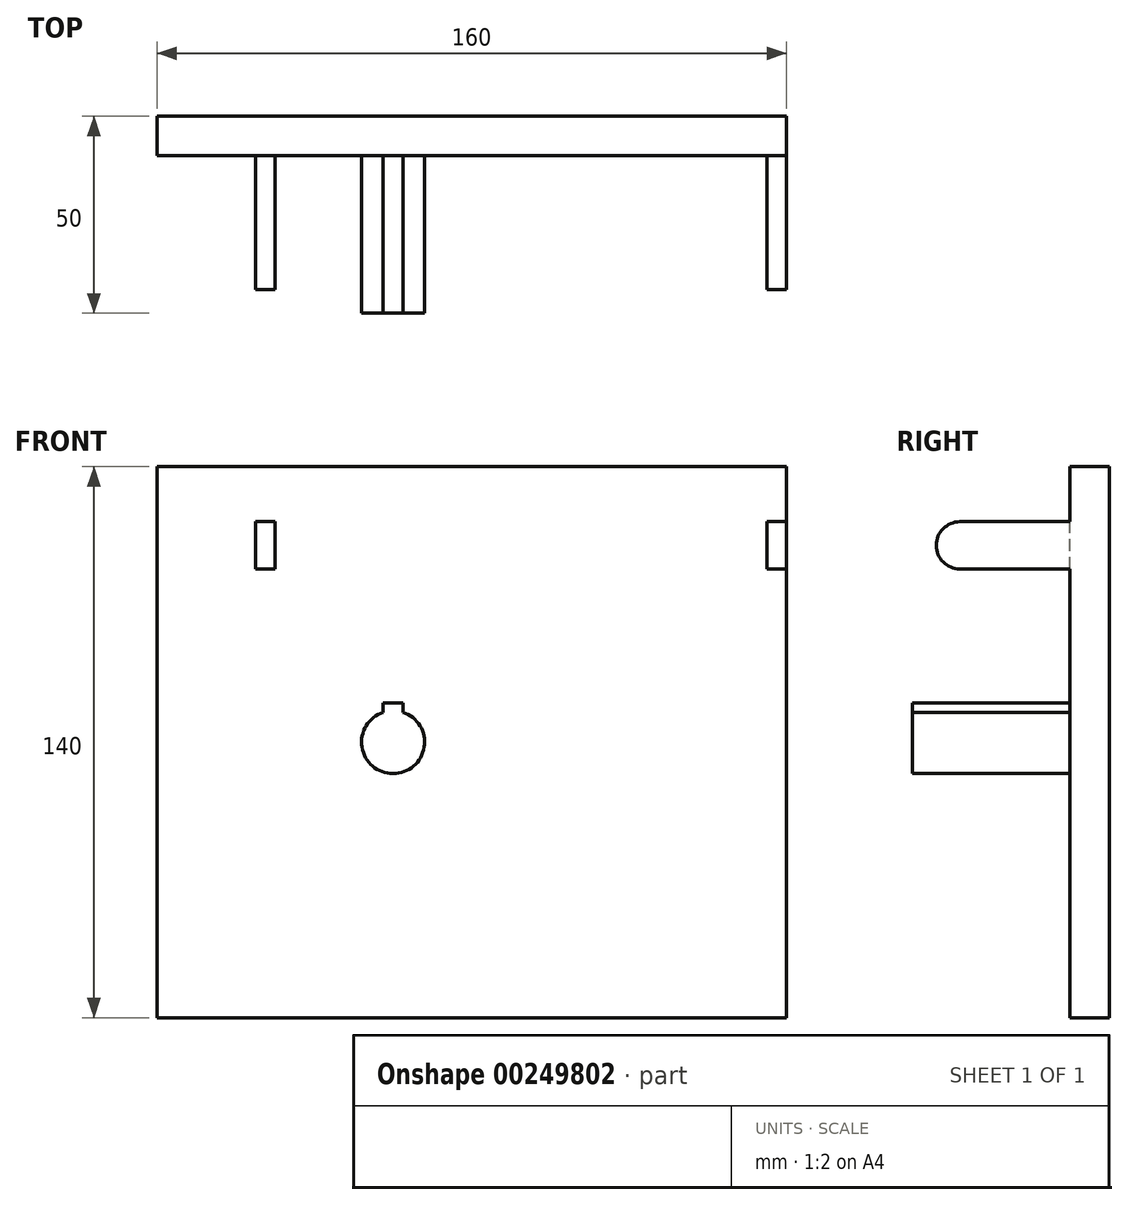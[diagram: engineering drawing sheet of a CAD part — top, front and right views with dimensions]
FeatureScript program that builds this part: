
annotation { "Feature Type Name" : "Feature", "Feature Type Description" : "" }
export const myFeature = defineFeature(function(context is Context, id is Id, definition is map)
    precondition{}
    {
        {
            var Q0;
            Q0=qCreatedBy(makeId("Front.planeOp"),FACE);
            var sketch = newSketch(context, id + "F0", { "sketchPlane" : qUnion([Q0])});
            skLineSegment(sketch, "E0.bottom", {"start": v(-60, 70) * mm, "end": v(100, 70) * mm});
            skLineSegment(sketch, "E0.top", {"start": v(-60, -70) * mm, "end": v(100, -70) * mm});
            skLineSegment(sketch, "E0.left", {"start": v(-60, 70) * mm, "end": v(-60, -70) * mm});
            skLineSegment(sketch, "E0.right", {"start": v(100, 70) * mm, "end": v(100, -70) * mm});
            skSolve(sketch);
        }
        {
            var Q0;
            Q0 = qSketchRegion(id + "F0", true);
            extrude(context, id + "F1", {"entities" : qUnion([Q0]), "oppositeDirection" : true, "depth" : 10 * mm});
        }
        {
            var Q0;
            Q0=makeQuery(id+"F1.opExtrude","CAP_FACE",FACE,{"disambiguationData":[OSD([sQuery(id+"F0.wireOp",EDGE,"E0.bottom"),sQuery(id+"F0.wireOp",EDGE,"E0.top"),sQuery(id+"F0.wireOp",EDGE,"E0.left"),sQuery(id+"F0.wireOp",EDGE,"E0.right")])],"isStart":true});
            var sketch = newSketch(context, id + "F2", { "sketchPlane" : qUnion([Q0])});
            skArc(sketch, "E1", {"start": v(-2.5, 7.6) * mm, "mid": v(0, -8) * mm, "end": v(2.5, 7.6) * mm});
            skLineSegment(sketch, "E2.bottom", {"start": v(-2.5, 10) * mm, "end": v(2.5, 10) * mm});
            skLineSegment(sketch, "E2.left", {"start": v(-2.5, 10) * mm, "end": v(-2.5, 7.6) * mm});
            skLineSegment(sketch, "E2.right", {"start": v(2.5, 10) * mm, "end": v(2.5, 7.6) * mm});
            skSolve(sketch);
        }
        {
            var Q0;
            Q0 = qSketchRegion(id + "F2", true);
            extrude(context, id + "F3", {"entities" : qUnion([Q0]), "operationType" : NewBodyOperationType.ADD, "depth" : 40 * mm});
        }
        {
            var Q0;
            Q0=makeQuery(id+"F1.opExtrude","SWEPT_FACE",FACE,{"disambiguationData":[OSD([sQuery(id+"F0.wireOp",EDGE,"E0.right")])]});
            var sketch = newSketch(context, id + "F4", { "sketchPlane" : qUnion([Q0])});
            skLineSegment(sketch, "E3", {"start": v(-35.66, 50) * mm, "end": v(16.18, 50) * mm, "construction": true});
            skLineSegment(sketch, "E4.0", {"start": v(-28, 44) * mm, "end": v(10, 44) * mm});
            skLineSegment(sketch, "E5.0", {"start": v(-28, 56) * mm, "end": v(10, 56) * mm});
            skArc(sketch, "E6", {"start": v(-28, 56) * mm, "mid": v(-34, 50) * mm, "end": v(-28, 44) * mm});
            skLineSegment(sketch, "E7", {"start": v(10, 56) * mm, "end": v(10, 44) * mm});
            skSolve(sketch);
        }
        {
            var Q0;
            Q0 = qSketchRegion(id + "F4", true);
            extrude(context, id + "F5", {"entities" : qUnion([Q0]), "operationType" : NewBodyOperationType.ADD, "oppositeDirection" : true, "depth" : 5 * mm});
        }
        {
            var Q0;
            Q0=qCreatedBy(makeId("Right.planeOp"),FACE);
            cPlane(context, id + "F6", {"entities" : qUnion([Q0]), "cplaneType" : CPlaneType.OFFSET, "offset" : 35 * mm, "oppositeDirection" : true, "width" : 150 * mm, "height" : 150 * mm});
        }
        {
            var Q0;
            Q0=qCreatedBy(id+"F6.planeOp",FACE);
            var sketch = newSketch(context, id + "F7", { "sketchPlane" : qUnion([Q0])});
            skArc(sketch, "E8.0", {"start": v(-28, 56) * mm, "mid": v(-34, 50) * mm, "end": v(-28, 44) * mm});
            skLineSegment(sketch, "E8.1", {"start": v(10, 56) * mm, "end": v(10, 44) * mm});
            skLineSegment(sketch, "E8.2", {"start": v(-35.66, 50) * mm, "end": v(16.18, 50) * mm});
            skLineSegment(sketch, "E8.3", {"start": v(-28, 44) * mm, "end": v(10, 44) * mm});
            skLineSegment(sketch, "E8.4", {"start": v(-28, 56) * mm, "end": v(10, 56) * mm});
            skSolve(sketch);
        }
        {
            var Q0;
            Q0 = qSketchRegion(id + "F7", true);
            extrude(context, id + "F8", {"entities" : qUnion([Q0]), "operationType" : NewBodyOperationType.ADD, "depth" : 5 * mm});
        }
    });
